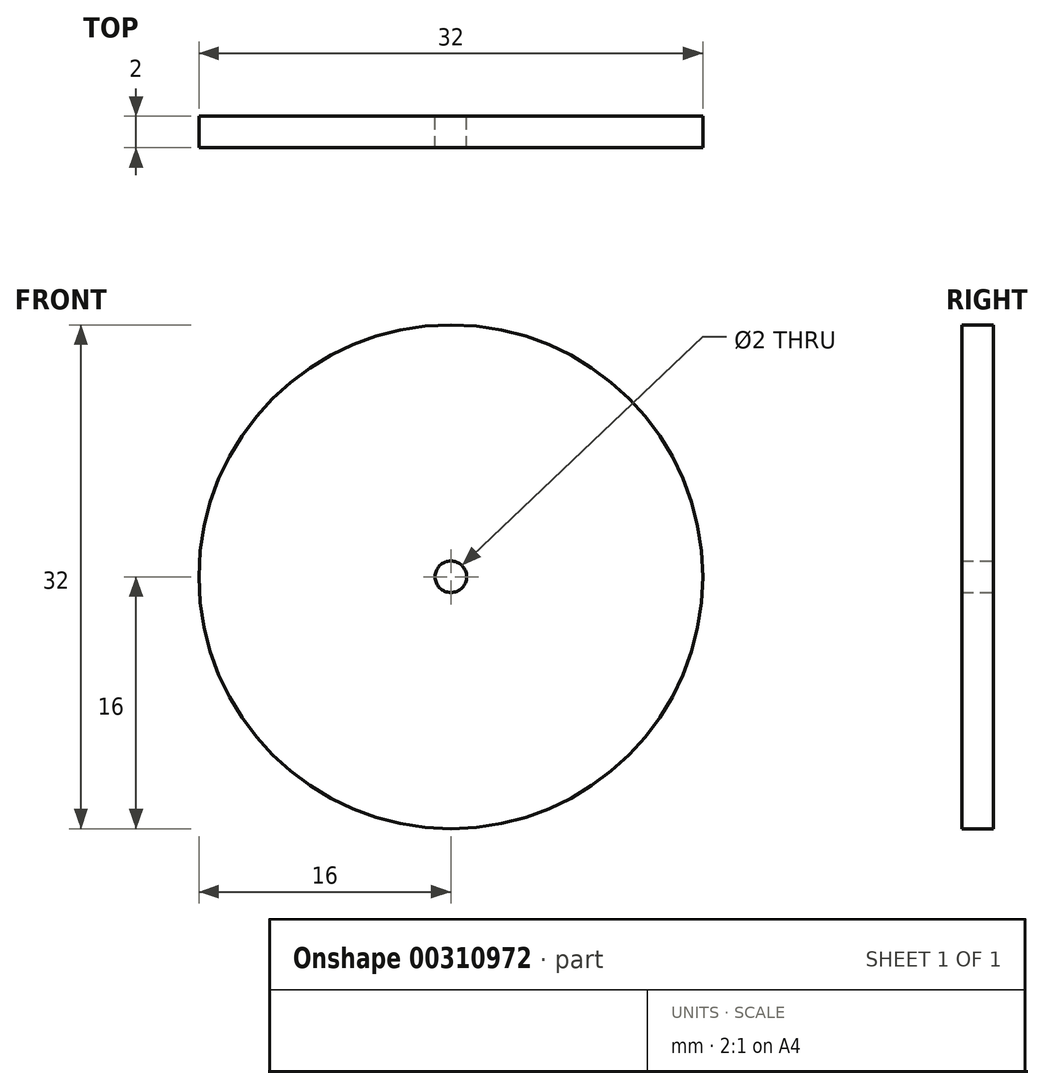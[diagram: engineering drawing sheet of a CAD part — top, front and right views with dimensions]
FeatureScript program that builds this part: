
annotation { "Feature Type Name" : "Feature", "Feature Type Description" : "" }
export const myFeature = defineFeature(function(context is Context, id is Id, definition is map)
    precondition{}
    {
        {
            var Q0;
            Q0=qCreatedBy(makeId("Front.planeOp"),FACE);
            var sketch = newSketch(context, id + "F0", { "sketchPlane" : qUnion([Q0])});
            skCircle(sketch, "E0", {"center": v(0, 0) * mm, "radius": 16 * mm});
            skCircle(sketch, "E1", {"center": v(0, 0) * mm, "radius": 1 * mm});
            skSolve(sketch);
        }
        {
            var Q0;
            Q0=makeQuery(id+"F0.imprint","IMPRINT",FACE,{"disambiguationData":[TD([[makeQuery(id+"F0.imprint","IMPRINT",EDGE,{"derivedFrom":sQuery(id+"F0.wireOp",EDGE,"E0")}),1.0]])]});
            extrude(context, id + "F1", {"entities" : qUnion([Q0]), "depth" : 2 * mm});
        }
    });
